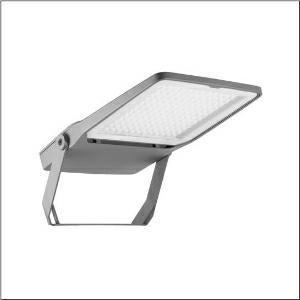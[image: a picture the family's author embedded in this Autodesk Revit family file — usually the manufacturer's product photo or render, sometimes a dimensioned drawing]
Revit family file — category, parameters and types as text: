
# Revit family: floodlight_fl_20_midi___pl61_5xa7682e1c1ac_6874
name_source: partatom
category: Lighting Fixtures
units: mm (PartAtom-declared; Revit-internal decimal feet)

## family parameters
Cut with Voids When Loaded = No
Host = Face
Light Source = No
Part Type = Normal
Room Calculation Point = No
Round Connector Dimension = Use Diameter
Shared = No

## types (1)
- --- (1 x LED 3000K / CRI = 80 (unbekannt), 21280 lm, 3000K)
    Apparent Load = 208 VA
    CIE Flux Codes = 33 65 98 100 100
    Color Rendering = 80
    Color Temperature = 3000K
    Default Elevation = 1800 mm
    Description = Floodlight FL 20 midi, floodlight, primary light control with lens, of plastic, primary optical cover: protective disc, of toughened safety glass, transparent, light distribution: PL61, light emission: direct distribution, primary light characteristic: asymmetric, installation type: surface-mounted, LED High Power LED, rated luminous flux: 21.280 lm, light colour: 830, colour temperature: 3000K, control gear: ECG Plus, control: flexible luminous flux parameterisation, time-dependent luminous flux control, digital communication interface, power reduction, overheat protection, electronic power reduction, with terminal, 5-pole, max. 2.5mm², mains connection: 220..240V, AC, 50/60Hz, rated input power: 208W, LED unit, of diecast aluminium, powder-coated, Siteco® metallic grey (DB 702S), length: 654 mm, width: 450 mm, height: 76mm, housing frame, of diecast aluminium, powder-coated, Siteco® metallic grey (DB 702S), mounting bracket, of steel, powder-coated, Siteco® metallic grey (DB 702S), DALIprotection rating (complete): IP66, insulation class (complete): insulation class II (safety insulation), certification: CE, ENEC, VDE, protection symbol: D, permissible ambient temperature for indoor applications: -40..+40°C, permissible ambient temperature for outdoor applications: -40..+50°C, standard: DIN EN 12944, packaging unit: 1 piece

Light Distribution: PL61
    Height = 76 mm
    Lamp = 1 x LED 3000K / CRI >= 80 (unbekannt)
    Lamp Light Flux = 21280 lm
    Lamp count = 1
    Length = 672 mm
    Luminous efficacy = 102 lm/W
    Manufacturer = Siteco
    ModVariant = No
    Model = 5XA7682E1C1AC
    Number of Poles = 1
    OnlyDefault = Yes
    Power Factor = 1
    Product Name = Floodlight FL 20 midi | PL61
    Product group = floodlight | pylon top
    ProductGroupID = 6101
    Protection Class = Protection class II
    Protection Degree = IP 66
    RLX_Detail_Level = 1
    RlxData = <blob elided: 97721 chars, md5=f467a0ce>
    Socket = socket
    Standby Power = 0 W
    System Light Flux = 21280 lm
    System Power = 208 W
    Type Comments = factory setting: luminous flux: 100 % | dim-lin: 254 | 484 mA
    Type Image = l_1005943.jpg
    URL = http://relux.com
    VarID = @adj_142427
    Voltage = 0 V
    Weight = 0.00 kg
    Width = 450 mm

## geometry (parser evidence)
native form markers: Blend x4, Sweep x12
no freeform markers — native parametric forms only
